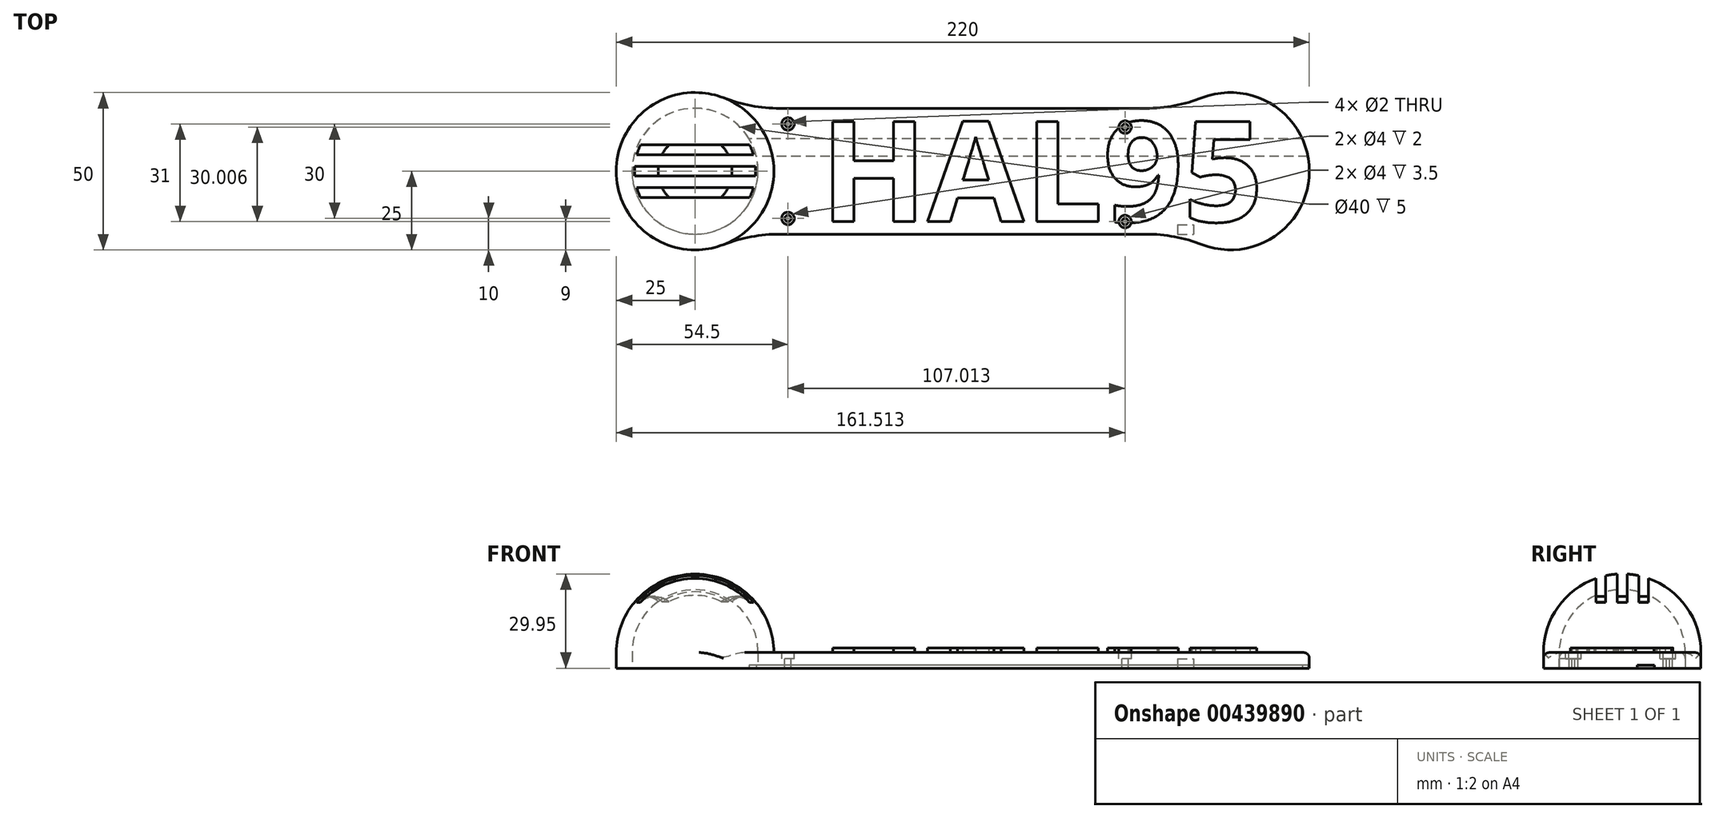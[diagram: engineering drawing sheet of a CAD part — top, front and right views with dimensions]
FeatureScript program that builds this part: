
annotation { "Feature Type Name" : "Feature", "Feature Type Description" : "" }
export const myFeature = defineFeature(function(context is Context, id is Id, definition is map)
    precondition{}
    {
        {
            var Q0;
            Q0=qCreatedBy(makeId("Top.planeOp"),FACE);
            var sketch = newSketch(context, id + "F0", { "sketchPlane" : qUnion([Q0])});
            skLineSegment(sketch, "E0.bottom", {"start": v(27, 10) * mm, "end": v(32, 10) * mm, "construction": true});
            skLineSegment(sketch, "E0.top", {"start": v(27, -10) * mm, "end": v(32, -10) * mm, "construction": true});
            skLineSegment(sketch, "E0.left", {"start": v(27, 10) * mm, "end": v(27, -10) * mm, "construction": true});
            skLineSegment(sketch, "E0.right", {"start": v(32, 10) * mm, "end": v(32, -10) * mm, "construction": true});
            skLineSegment(sketch, "E1.1.0.0", {"start": v(197, -10) * mm, "end": v(202, -10) * mm, "construction": true});
            skLineSegment(sketch, "E1.1.0.1", {"start": v(197, 10) * mm, "end": v(202, 10) * mm, "construction": true});
            skLineSegment(sketch, "E1.1.0.2", {"start": v(202, 10) * mm, "end": v(202, -10) * mm, "construction": true});
            skLineSegment(sketch, "E1.1.0.3", {"start": v(197, 10) * mm, "end": v(197, -10) * mm, "construction": true});
            skCircle(sketch, "E2.1.0.0", {"center": v(170, 0) * mm, "radius": 25 * mm});
            skLineSegment(sketch, "E3.bottom", {"start": v(140.7, -17) * mm, "end": v(180.7, -17) * mm, "construction": true});
            skLineSegment(sketch, "E3.top", {"start": v(140.7, -22) * mm, "end": v(180.7, -22) * mm, "construction": true});
            skLineSegment(sketch, "E3.left", {"start": v(140.7, -17) * mm, "end": v(140.7, -22) * mm, "construction": true});
            skLineSegment(sketch, "E3.right", {"start": v(180.7, -17) * mm, "end": v(180.7, -22) * mm, "construction": true});
            skLineSegment(sketch, "E4", {"start": v(15, -20) * mm, "end": v(155, -20) * mm});
            skLineSegment(sketch, "E5", {"start": v(15, 20) * mm, "end": v(155, 20) * mm});
            skLineSegment(sketch, "E6", {"start": v(254.3, 0) * mm, "end": v(-36.3, 0) * mm, "construction": true});
            skLineSegment(sketch, "E7", {"start": v(29.5, 22.1) * mm, "end": v(29.5, -23.24) * mm, "construction": true});
            skPoint(sketch, "E7.endSnap0", {"position": v(29.5, -10) * mm});
            skLineSegment(sketch, "E8", {"start": v(140.7, -19.5) * mm, "end": v(180.7, -19.5) * mm, "construction": true});
            skCircle(sketch, "E9", {"center": v(0, 0) * mm, "radius": 25 * mm});
            skCircle(sketch, "E10", {"center": v(0, 0) * mm, "radius": 20 * mm});
            skLineSegment(sketch, "E11.bottom", {"start": v(24.5, 20) * mm, "end": v(34.5, 20) * mm, "construction": true});
            skLineSegment(sketch, "E11.top", {"start": v(24.5, 10) * mm, "end": v(34.5, 10) * mm, "construction": true});
            skLineSegment(sketch, "E11.left", {"start": v(24.5, 20) * mm, "end": v(24.5, 10) * mm, "construction": true});
            skLineSegment(sketch, "E11.right", {"start": v(34.5, 20) * mm, "end": v(34.5, 10) * mm, "construction": true});
            skLineSegment(sketch, "E12.MirrorCS", {"start": v(24.5, -20) * mm, "end": v(34.5, -20) * mm, "construction": true});
            skLineSegment(sketch, "E13.MirrorCS", {"start": v(34.5, -20) * mm, "end": v(34.5, -10) * mm, "construction": true});
            skLineSegment(sketch, "E14.MirrorCS", {"start": v(24.5, -10) * mm, "end": v(34.5, -10) * mm, "construction": true});
            skLineSegment(sketch, "E15.MirrorCS", {"start": v(24.5, -20) * mm, "end": v(24.5, -10) * mm, "construction": true});
            skSolve(sketch);
        }
        {
            var Q0;
            {var subQ0=sQuery(id+"F0.wireOp",EDGE,"E4");Q0=makeQuery(id+"F0.imprint","IMPRINT",FACE,{"disambiguationData":[TD([[makeQuery(id+"F0.imprint","IMPRINT",EDGE,{"derivedFrom":subQ0}),1.0]])]});}
            var Q1;
            Q1=makeQuery(id+"F0.imprint","IMPRINT",FACE,{"disambiguationData":[TD([[makeQuery(id+"F0.imprint","IMPRINT",EDGE,{"derivedFrom":sQuery(id+"F0.wireOp",EDGE,"E10")}),-1.0]])]});
            var Q2;
            {var subQ0=sQuery(id+"F0.wireOp",EDGE,"E2.1.0.0");var subQ1=makeQuery(id+"F0.imprint","INTERSECT",VERTEX,{"derivedFrom":[subQ0,sQuery(id+"F0.wireOp",EDGE,"E4")]});Q2=makeQuery(id+"F0.imprint","IMPRINT",FACE,{"disambiguationData":[TD([[makeQuery(id+"F0.imprint","IMPRINT",EDGE,{"disambiguationData":[TD([[subQ1,1.0]])],"derivedFrom":subQ0}),1.0]])]});}
            extrude(context, id + "F1", {"entities" : qUnion([Q0, Q1, Q2]), "depth" : 5 * mm});
        }
        {
            var Q0;
            Q0=makeQuery(id+"F1.opExtrude","CAP_FACE",FACE,{"disambiguationData":[OSD([sQuery(id+"F0.wireOp",EDGE,"E2.1.0.0"),sQuery(id+"F0.wireOp",EDGE,"E4"),sQuery(id+"F0.wireOp",EDGE,"E5"),sQuery(id+"F0.wireOp",EDGE,"E9"),sQuery(id+"F0.wireOp",EDGE,"E10")])],"isStart":false});
            var sketch = newSketch(context, id + "F2", { "sketchPlane" : qUnion([Q0])});
            skCircle(sketch, "E16", {"center": v(29.5, 15) * mm, "radius": 0.88 * mm, "construction": true});
            skCircle(sketch, "E17.MirrorC", {"center": v(29.5, -15) * mm, "radius": 0.88 * mm, "construction": true});
            skText(sketch, "E18", { "text": "HAL95", "fontName": "OpenSans-Bold.ttf"});
            skLineSegment(sketch, "E19", {"start": v(29.5, -15) * mm, "end": v(29.5, 15) * mm, "construction": true});
            const initialGuessF2  = {"E18": [0.03975, -0.016, 1, 0, 0.032]};
            skSetInitialGuess(sketch, initialGuessF2);
            skSolve(sketch);
        }
        {
            var Q0;
            Q0=makeQuery(id+"F1.opExtrude","CAP_FACE",FACE,{"disambiguationData":[OSD([sQuery(id+"F0.wireOp",EDGE,"E2.1.0.0"),sQuery(id+"F0.wireOp",EDGE,"E4"),sQuery(id+"F0.wireOp",EDGE,"E5"),sQuery(id+"F0.wireOp",EDGE,"E9"),sQuery(id+"F0.wireOp",EDGE,"E10")])],"isStart":false});
            var sketch = newSketch(context, id + "F3", { "sketchPlane" : qUnion([Q0])});
            skLineSegment(sketch, "E20.bottom", {"start": v(140.51, -17) * mm, "end": v(180.51, -17) * mm, "construction": true});
            skLineSegment(sketch, "E20.top", {"start": v(132.51, -23.4) * mm, "end": v(180.51, -23.4) * mm, "construction": true});
            skLineSegment(sketch, "E20.left", {"start": v(140.51, -17) * mm, "end": v(140.51, -22) * mm, "construction": true});
            skLineSegment(sketch, "E20.right", {"start": v(180.51, -17) * mm, "end": v(180.51, -23.4) * mm, "construction": true});
            skLineSegment(sketch, "E21", {"start": v(140.51, -19.5) * mm, "end": v(136.51, -19.5) * mm, "construction": true});
            skLineSegment(sketch, "E22", {"start": v(136.51, -4.3) * mm, "end": v(136.51, 14) * mm, "construction": true});
            skCircle(sketch, "E23", {"center": v(136.51, 14) * mm, "radius": 4 * mm, "construction": true});
            skLineSegment(sketch, "E24", {"start": v(140.51, -17) * mm, "end": v(140.51, -1.2) * mm, "construction": true});
            skLineSegment(sketch, "E25.MirrorCS", {"start": v(132.51, -23.4) * mm, "end": v(132.51, -1.2) * mm, "construction": true});
            skPoint(sketch, "E26.orphan", {"position": v(132.51, -17) * mm});
            skPoint(sketch, "E27.orphan", {"position": v(132.51, -5.2) * mm});
            skPoint(sketch, "E28.orphan", {"position": v(140.51, -5.2) * mm});
            skCircle(sketch, "E29.0.1.0", {"center": v(136.51, -16) * mm, "radius": 4 * mm, "construction": true});
            skLineSegment(sketch, "E29.direction2", {"start": v(136.51, 14) * mm, "end": v(136.51, -16) * mm, "construction": true});
            skSolve(sketch);
        }
        {
            var Q0;
            Q0=sQuery(id+"F2.wireOp",VERTEX,"E16.center");
            var Q1;
            Q1=sQuery(id+"F2.wireOp",VERTEX,"E17.MirrorC.center");
            var Q2;
            Q2=makeQuery(id+"F1.opExtrude","SWEPT_BODY",BODY,{"disambiguationData":[OSD([sQuery(id+"F0.wireOp",EDGE,"E2.1.0.0"),sQuery(id+"F0.wireOp",EDGE,"E4"),sQuery(id+"F0.wireOp",EDGE,"E5"),sQuery(id+"F0.wireOp",EDGE,"E9"),sQuery(id+"F0.wireOp",EDGE,"E10")])]});
            hole(context, id + "F4", {"style" : HoleStyle.C_BORE, "endStyle" : HoleEndStyle.BLIND, "holeDiameter" : 2 * mm, "cBoreDiameter" : 4 * mm, "cBoreDepth" : 2 * mm, "holeDepth" : 5 * mm, "isTappedThrough" : true, "tappedDepth" : 12 * mm, "tapClearance" : 3, "startFromSketch" : true, "locations" : qUnion([Q0, Q1]), "scope" : qUnion([Q2])});
        }
        {
            var Q0;
            Q0=sQuery(id+"F3.wireOp",VERTEX,"E22.end");
            var Q1;
            Q1=sQuery(id+"F3.wireOp",VERTEX,"E29.direction2.end");
            var Q2;
            Q2=makeQuery(id+"F1.opExtrude","SWEPT_BODY",BODY,{"disambiguationData":[OSD([sQuery(id+"F0.wireOp",EDGE,"E2.1.0.0"),sQuery(id+"F0.wireOp",EDGE,"E4"),sQuery(id+"F0.wireOp",EDGE,"E5"),sQuery(id+"F0.wireOp",EDGE,"E9"),sQuery(id+"F0.wireOp",EDGE,"E10")])]});
            hole(context, id + "F5", {"style" : HoleStyle.C_BORE, "endStyle" : HoleEndStyle.BLIND, "holeDiameter" : 2 * mm, "cBoreDiameter" : 4 * mm, "cBoreDepth" : 2 * mm, "holeDepth" : 5 * mm, "isTappedThrough" : true, "tappedDepth" : 12 * mm, "tapClearance" : 3, "startFromSketch" : true, "locations" : qUnion([Q0, Q1]), "scope" : qUnion([Q2])});
        }
        {
            var Q0;
            Q0=qCreatedBy(makeId("Top.planeOp"),FACE);
            cPlane(context, id + "F6", {"entities" : qUnion([Q0]), "cplaneType" : CPlaneType.OFFSET, "offset" : 30 * mm, "width" : 150 * mm, "height" : 150 * mm});
        }
        {
            var Q0;
            Q0=qCreatedBy(id+"F6.planeOp",FACE);
            var sketch = newSketch(context, id + "F7", { "sketchPlane" : qUnion([Q0])});
            skCircle(sketch, "E30", {"center": v(0, 0) * mm, "radius": 11.73 * mm});
            skPoint(sketch, "E31.endSnap0", {"position": v(0, 10.2) * mm});
            skLineSegment(sketch, "E32", {"start": v(-11.63, 1.55) * mm, "end": v(11.63, 1.55) * mm});
            skLineSegment(sketch, "E33.0.1.0", {"start": v(-10.5, 5.25) * mm, "end": v(10.5, 5.25) * mm});
            skLineSegment(sketch, "E33.0.2.0", {"start": v(-8.25, 8.34) * mm, "end": v(8.25, 8.34) * mm});
            skLineSegment(sketch, "E33.0.3.0", {"start": v(-11.63, -1.54) * mm, "end": v(11.63, -1.54) * mm});
            skLineSegment(sketch, "E33.0.4.0", {"start": v(-10.5, -5.24) * mm, "end": v(10.5, -5.24) * mm});
            skLineSegment(sketch, "E33.0.5.0", {"start": v(-8.26, -8.33) * mm, "end": v(8.26, -8.33) * mm});
            skSolve(sketch);
        }
        {
            var Q0;
            Q0=makeQuery(id+"F1.opExtrude","CAP_FACE",FACE,{"disambiguationData":[OSD([sQuery(id+"F0.wireOp",EDGE,"E2.1.0.0"),sQuery(id+"F0.wireOp",EDGE,"E4"),sQuery(id+"F0.wireOp",EDGE,"E5"),sQuery(id+"F0.wireOp",EDGE,"E9"),sQuery(id+"F0.wireOp",EDGE,"E10")])],"isStart":false});
            var sketch = newSketch(context, id + "F8", { "sketchPlane" : qUnion([Q0])});
            skArc(sketch, "E34", {"start": v(20, 0) * mm, "mid": v(0, 20) * mm, "end": v(-20, 0) * mm});
            skLineSegment(sketch, "E35", {"start": v(-25, 0) * mm, "end": v(25, 0) * mm});
            skArc(sketch, "E36", {"start": v(25, 0) * mm, "mid": v(0, 25) * mm, "end": v(-25, 0) * mm});
            skSolve(sketch);
        }
        {
            var Q0;
            {var subQ4=sQuery(id+"F8.wireOp",EDGE,"E34");Q0=makeQuery(id+"F8.imprint","IMPRINT",FACE,{"disambiguationData":[TD([[makeQuery(id+"F8.imprint","IMPRINT",EDGE,{"derivedFrom":subQ4}),-1.0]])]});}
            var Q1;
            Q1=sQuery(id+"F8.wireOp",EDGE,"E35");
            revolve(context, id + "F9", {"operationType" : NewBodyOperationType.ADD, "entities" : qUnion([Q0]), "axis" : qUnion([Q1]), "revolveType" : RevolveType.ONE_DIRECTION, "angle" : 180 * degree});
        }
        {
            var Q0;
            {var subQ0=sQuery(id+"F7.wireOp",EDGE,"E33.0.1.0");Q0=makeQuery(id+"F7.imprint","IMPRINT",FACE,{"disambiguationData":[TD([[makeQuery(id+"F7.imprint","IMPRINT",EDGE,{"derivedFrom":subQ0}),1.0]])]});}
            var Q1;
            {var subQ0=sQuery(id+"F7.wireOp",EDGE,"E32");Q1=makeQuery(id+"F7.imprint","IMPRINT",FACE,{"disambiguationData":[TD([[makeQuery(id+"F7.imprint","IMPRINT",EDGE,{"derivedFrom":subQ0}),-1.0]])]});}
            var Q2;
            {var subQ0=sQuery(id+"F7.wireOp",EDGE,"E33.0.4.0");Q2=makeQuery(id+"F7.imprint","IMPRINT",FACE,{"disambiguationData":[TD([[makeQuery(id+"F7.imprint","IMPRINT",EDGE,{"derivedFrom":subQ0}),-1.0]])]});}
            extrude(context, id + "F10", {"entities" : qUnion([Q0, Q1, Q2]), "operationType" : NewBodyOperationType.REMOVE, "oppositeDirection" : true, "depth" : 25 * mm});
        }
        {
            var Q0;
            {var subQ0=sQuery(id+"F7.wireOp",EDGE,"E30");Q0=makeQuery(id+"F10.boolean.opBoolean","INTERSECT",EDGE,{"derivedFrom":[makeQuery(id+"F9.opRevolve","SWEPT_FACE",FACE,{"disambiguationData":[OSD([sQuery(id+"F8.wireOp",EDGE,"E36")])]}),makeQuery(id+"F10.opExtrude","SWEPT_FACE",FACE,{"disambiguationData":[OSD([subQ0]),TDD([makeQuery(id+"F7.imprint","IMPRINT",EDGE,{"disambiguationData":[TD([[makeQuery(id+"F7.imprint","INTERSECT",VERTEX,{"disambiguationData":[OD(0.0)],"derivedFrom":[subQ0,sQuery(id+"F7.wireOp",EDGE,"E33.0.1.0")]}),1.0]])],"derivedFrom":subQ0})])]})]});}
            var Q1;
            {var subQ0=sQuery(id+"F7.wireOp",EDGE,"E30");Q1=makeQuery(id+"F10.boolean.opBoolean","INTERSECT",EDGE,{"derivedFrom":[makeQuery(id+"F9.opRevolve","SWEPT_FACE",FACE,{"disambiguationData":[OSD([sQuery(id+"F8.wireOp",EDGE,"E36")])]}),makeQuery(id+"F10.opExtrude","SWEPT_FACE",FACE,{"disambiguationData":[OSD([subQ0]),TDD([makeQuery(id+"F7.imprint","IMPRINT",EDGE,{"disambiguationData":[TD([[makeQuery(id+"F7.imprint","INTERSECT",VERTEX,{"disambiguationData":[OD(1.0)],"derivedFrom":[subQ0,sQuery(id+"F7.wireOp",EDGE,"E33.0.1.0")]}),-1.0]])],"derivedFrom":subQ0})])]})]});}
            var Q2;
            {var subQ0=sQuery(id+"F7.wireOp",EDGE,"E30");Q2=makeQuery(id+"F10.boolean.opBoolean","INTERSECT",EDGE,{"derivedFrom":[makeQuery(id+"F9.opRevolve","SWEPT_FACE",FACE,{"disambiguationData":[OSD([sQuery(id+"F8.wireOp",EDGE,"E36")])]}),makeQuery(id+"F10.opExtrude","SWEPT_FACE",FACE,{"disambiguationData":[OSD([subQ0]),TDD([makeQuery(id+"F7.imprint","IMPRINT",EDGE,{"disambiguationData":[TD([[makeQuery(id+"F7.imprint","INTERSECT",VERTEX,{"disambiguationData":[OD(0.0)],"derivedFrom":[subQ0,sQuery(id+"F7.wireOp",EDGE,"E32")]}),-1.0]])],"derivedFrom":subQ0})])]})]});}
            var Q3;
            {var subQ0=sQuery(id+"F7.wireOp",EDGE,"E30");Q3=makeQuery(id+"F10.boolean.opBoolean","INTERSECT",EDGE,{"derivedFrom":[makeQuery(id+"F9.opRevolve","SWEPT_FACE",FACE,{"disambiguationData":[OSD([sQuery(id+"F8.wireOp",EDGE,"E36")])]}),makeQuery(id+"F10.opExtrude","SWEPT_FACE",FACE,{"disambiguationData":[OSD([subQ0]),TDD([makeQuery(id+"F7.imprint","IMPRINT",EDGE,{"disambiguationData":[TD([[makeQuery(id+"F7.imprint","INTERSECT",VERTEX,{"disambiguationData":[OD(0.0)],"derivedFrom":[subQ0,sQuery(id+"F7.wireOp",EDGE,"E33.0.4.0")]}),-1.0]])],"derivedFrom":subQ0})])]})]});}
            var Q4;
            {var subQ0=sQuery(id+"F7.wireOp",EDGE,"E30");Q4=makeQuery(id+"F10.boolean.opBoolean","INTERSECT",EDGE,{"derivedFrom":[makeQuery(id+"F9.opRevolve","SWEPT_FACE",FACE,{"disambiguationData":[OSD([sQuery(id+"F8.wireOp",EDGE,"E36")])]}),makeQuery(id+"F10.opExtrude","SWEPT_FACE",FACE,{"disambiguationData":[OSD([subQ0]),TDD([makeQuery(id+"F7.imprint","IMPRINT",EDGE,{"disambiguationData":[TD([[makeQuery(id+"F7.imprint","INTERSECT",VERTEX,{"disambiguationData":[OD(1.0)],"derivedFrom":[subQ0,sQuery(id+"F7.wireOp",EDGE,"E33.0.4.0")]}),1.0]])],"derivedFrom":subQ0})])]})]});}
            var Q5;
            {var subQ0=sQuery(id+"F7.wireOp",EDGE,"E30");Q5=makeQuery(id+"F10.boolean.opBoolean","INTERSECT",EDGE,{"derivedFrom":[makeQuery(id+"F9.opRevolve","SWEPT_FACE",FACE,{"disambiguationData":[OSD([sQuery(id+"F8.wireOp",EDGE,"E36")])]}),makeQuery(id+"F10.opExtrude","SWEPT_FACE",FACE,{"disambiguationData":[OSD([subQ0]),TDD([makeQuery(id+"F7.imprint","IMPRINT",EDGE,{"disambiguationData":[TD([[makeQuery(id+"F7.imprint","INTERSECT",VERTEX,{"disambiguationData":[OD(1.0)],"derivedFrom":[subQ0,sQuery(id+"F7.wireOp",EDGE,"E32")]}),1.0]])],"derivedFrom":subQ0})])]})]});}
            fillet(context, id + "F11", {"entities" : qUnion([Q0, Q1, Q2, Q3, Q4, Q5]), "radius" : 5 * mm, "tangentPropagation" : true, "allowEdgeOverflow" : false});
        }
        {
            var Q0;
            Q0=qSketchRegion(id+"F2",true);
            extrude(context, id + "F12", {"entities" : qUnion([Q0]), "operationType" : NewBodyOperationType.ADD, "depth" : 1.5 * mm, "offsetDistance" : 25 * mm});
        }
        {
            var Q0;
            Q0=makeQuery(id+"F1.opExtrude","SWEPT_EDGE",EDGE,{"disambiguationData":[OSD([sQuery(id+"F0.wireOp",EDGE,"E5"),sQuery(id+"F0.wireOp",EDGE,"E9")])]});
            var Q1;
            Q1=makeQuery(id+"F1.opExtrude","SWEPT_EDGE",EDGE,{"disambiguationData":[OSD([sQuery(id+"F0.wireOp",EDGE,"E4"),sQuery(id+"F0.wireOp",EDGE,"E9")])]});
            var Q2;
            Q2=makeQuery(id+"F1.opExtrude","SWEPT_EDGE",EDGE,{"disambiguationData":[OSD([sQuery(id+"F0.wireOp",EDGE,"E2.1.0.0"),sQuery(id+"F0.wireOp",EDGE,"E5")])]});
            var Q3;
            Q3=makeQuery(id+"F1.opExtrude","SWEPT_EDGE",EDGE,{"disambiguationData":[OSD([sQuery(id+"F0.wireOp",EDGE,"E2.1.0.0"),sQuery(id+"F0.wireOp",EDGE,"E4")])]});
            fillet(context, id + "F13", {"entities" : qUnion([Q0, Q1, Q2, Q3]), "radius" : 50 * mm, "tangentPropagation" : true, "allowEdgeOverflow" : false});
        }
        {
            var Q0;
            {var subQ0=sQuery(id+"F0.wireOp",EDGE,"E4");var subQ1=sQuery(id+"F0.wireOp",EDGE,"E2.1.0.0");var subQ2=sQuery(id+"F0.wireOp",EDGE,"E9");var subQ3=sQuery(id+"F0.wireOp",EDGE,"E5");Q0=makeQuery(id+"F13.opFillet","BLEND_EDGE",EDGE,{"blendedFrom":[makeQuery(id+"F1.opExtrude","SWEPT_EDGE",EDGE,{"disambiguationData":[OSD([subQ3,subQ2])]}),makeQuery(id+"F12.boolean.opBoolean","SPLIT",FACE,{"disambiguationData":[TD([makeQuery(id+"F1.opExtrude","SWEPT_FACE",FACE,{"disambiguationData":[OSD([subQ1])]})])],"derivedFrom":makeQuery(id+"F1.opExtrude","CAP_FACE",FACE,{"disambiguationData":[OSD([subQ1,subQ0,subQ3,subQ2,sQuery(id+"F0.wireOp",EDGE,"E10")])],"isStart":false})})],"blendedInto":[makeQuery(id+"F12.boolean.opBoolean","SPLIT",FACE,{"disambiguationData":[TD([makeQuery(id+"F1.opExtrude","SWEPT_FACE",FACE,{"disambiguationData":[OSD([subQ1])]})])],"derivedFrom":makeQuery(id+"F1.opExtrude","CAP_FACE",FACE,{"disambiguationData":[OSD([subQ1,subQ0,subQ3,subQ2,sQuery(id+"F0.wireOp",EDGE,"E10")])],"isStart":false})})]});}
            fillet(context, id + "F14", {"entities" : qUnion([Q0]), "radius" : 1.8 * mm, "tangentPropagation" : true, "allowEdgeOverflow" : false});
        }
        {
            var Q0;
            Q0=qCreatedBy(makeId("Top.planeOp"),FACE);
            var sketch = newSketch(context, id + "F15", { "sketchPlane" : qUnion([Q0])});
            skLineSegment(sketch, "E37", {"start": v(0, 0) * mm, "end": v(170, 0) * mm, "construction": true});
            skLineSegment(sketch, "E38.MirrorCS", {"start": v(158.21, -17) * mm, "end": v(158.21, -20) * mm});
            skLineSegment(sketch, "E39.MirrorCS", {"start": v(153.21, -17) * mm, "end": v(153.21, -20) * mm});
            skLineSegment(sketch, "E40.MirrorCS", {"start": v(153.21, -17) * mm, "end": v(158.21, -17) * mm});
            skLineSegment(sketch, "E41.MirrorCS", {"start": v(153.21, -20) * mm, "end": v(158.21, -20) * mm});
            skLineSegment(sketch, "E42.MirrorCS", {"start": v(139.01, -17) * mm, "end": v(158.21, -17) * mm, "construction": true});
            skLineSegment(sketch, "E43.MirrorCS", {"start": v(170, 0) * mm, "end": v(139.01, -17) * mm, "construction": true});
            skSolve(sketch);
        }
        {
            var Q0;
            Q0 = qSketchRegion(id + "F15", true);
            extrude(context, id + "F16", {"entities" : qUnion([Q0]), "operationType" : NewBodyOperationType.REMOVE, "depth" : 3 * mm});
        }
        {
            var Q0;
            Q0=qCreatedBy(makeId("Top.planeOp"),FACE);
            var sketch = newSketch(context, id + "F17", { "sketchPlane" : qUnion([Q0])});
            skLineSegment(sketch, "E44.bottom", {"start": v(195.1, 10.24) * mm, "end": v(14.74, 10.24) * mm});
            skLineSegment(sketch, "E44.top", {"start": v(195.1, 4.74) * mm, "end": v(14.74, 4.74) * mm});
            skLineSegment(sketch, "E44.left", {"start": v(195.1, 10.24) * mm, "end": v(195.1, 4.74) * mm});
            skLineSegment(sketch, "E44.right", {"start": v(14.74, 10.24) * mm, "end": v(14.74, 4.74) * mm});
            skSolve(sketch);
        }
        {
            var Q0;
            Q0=makeQuery(id+"F17.imprint","IMPRINT",FACE,{"disambiguationData":[TD([[makeQuery(id+"F17.imprint","IMPRINT",EDGE,{"derivedFrom":sQuery(id+"F17.wireOp",EDGE,"E44.bottom")}),1.0]])]});
            extrude(context, id + "F18", {"entities" : qUnion([Q0]), "operationType" : NewBodyOperationType.REMOVE, "depth" : 1 * mm, "offsetDistance" : 25 * mm});
        }
        {
            var Q0;
            Q0=sQuery(id+"F3.wireOp",VERTEX,"E22.end");
            var Q1;
            Q1=sQuery(id+"F3.wireOp",VERTEX,"E29.direction2.end");
            var Q2;
            Q2=makeQuery(id+"F1.opExtrude","SWEPT_BODY",BODY,{"disambiguationData":[OSD([sQuery(id+"F0.wireOp",EDGE,"E2.1.0.0"),sQuery(id+"F0.wireOp",EDGE,"E4"),sQuery(id+"F0.wireOp",EDGE,"E5"),sQuery(id+"F0.wireOp",EDGE,"E9"),sQuery(id+"F0.wireOp",EDGE,"E10")])]});
            hole(context, id + "F19", {"style" : HoleStyle.C_BORE, "endStyle" : HoleEndStyle.BLIND, "oppositeDirection" : true, "holeDiameter" : 2 * mm, "cBoreDiameter" : 4 * mm, "cBoreDepth" : 2 * mm, "holeDepth" : 5 * mm, "isTappedThrough" : true, "tappedDepth" : 12 * mm, "tapClearance" : 3, "startFromSketch" : true, "locations" : qUnion([Q0, Q1]), "scope" : qUnion([Q2])});
        }
    });
